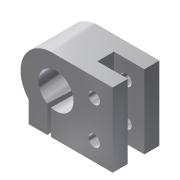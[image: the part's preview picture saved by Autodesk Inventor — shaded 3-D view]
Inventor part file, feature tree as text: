
AUTODESK INVENTOR PART (.ipt)
format: ipt  version: 2015 (Build 190159000, 159)  size: 159,232 bytes
history: native  units: mm
features: sketch x4, extrude x3, revolve x1
ambient origin geometry x8: Origin, YZ Plane, XZ Plane, XY Plane, X Axis, Y Axis, Z Axis, Center Point
bodies: Solid1 (feature_tree)
feature tree (8):
  extrude  "Extrusion1"  Depth=40.0mm
  extrude  "Extrusion2"  Depth=10.0mm
  revolve  "Revolution1"  [1 undecoded]
  extrude  "Extrusion3"  Depth=45.5mm
  sketch  "Sketch1"  dims[d0=50.0mm d1=40.0mm]
  sketch  "Sketch2"  dims[d2=10.0mm d3=10.0mm]
  sketch  "Sketch5"  dims[d4=20.0mm d5=6.2mm]
  sketch  "Sketch6"  dims[d6=6.2mm d7=45.5mm d8=35.5mm d9=4.5mm d10=4.5mm d13=12.5mm d14=12.5mm d15=2.0mm d16=25.4mm d17=0.0mm d18=8.2mm d19=16.5mm d20=9.0mm d21=25.4mm d22=0.0mm d23=10.0mm d25=9.5mm d26=30.543262mm d27=10.0mm d28=19.0mm d29=30.0mm d30=90.0deg d31=19.0mm d32=90.0deg d33=10.0mm d34=0.0mm]
note: 1 required parameter value undecoded (feature->parameter linkage not recoverable at this tier; creation-order binding heuristic only, values carry confidence <= 0.55)
